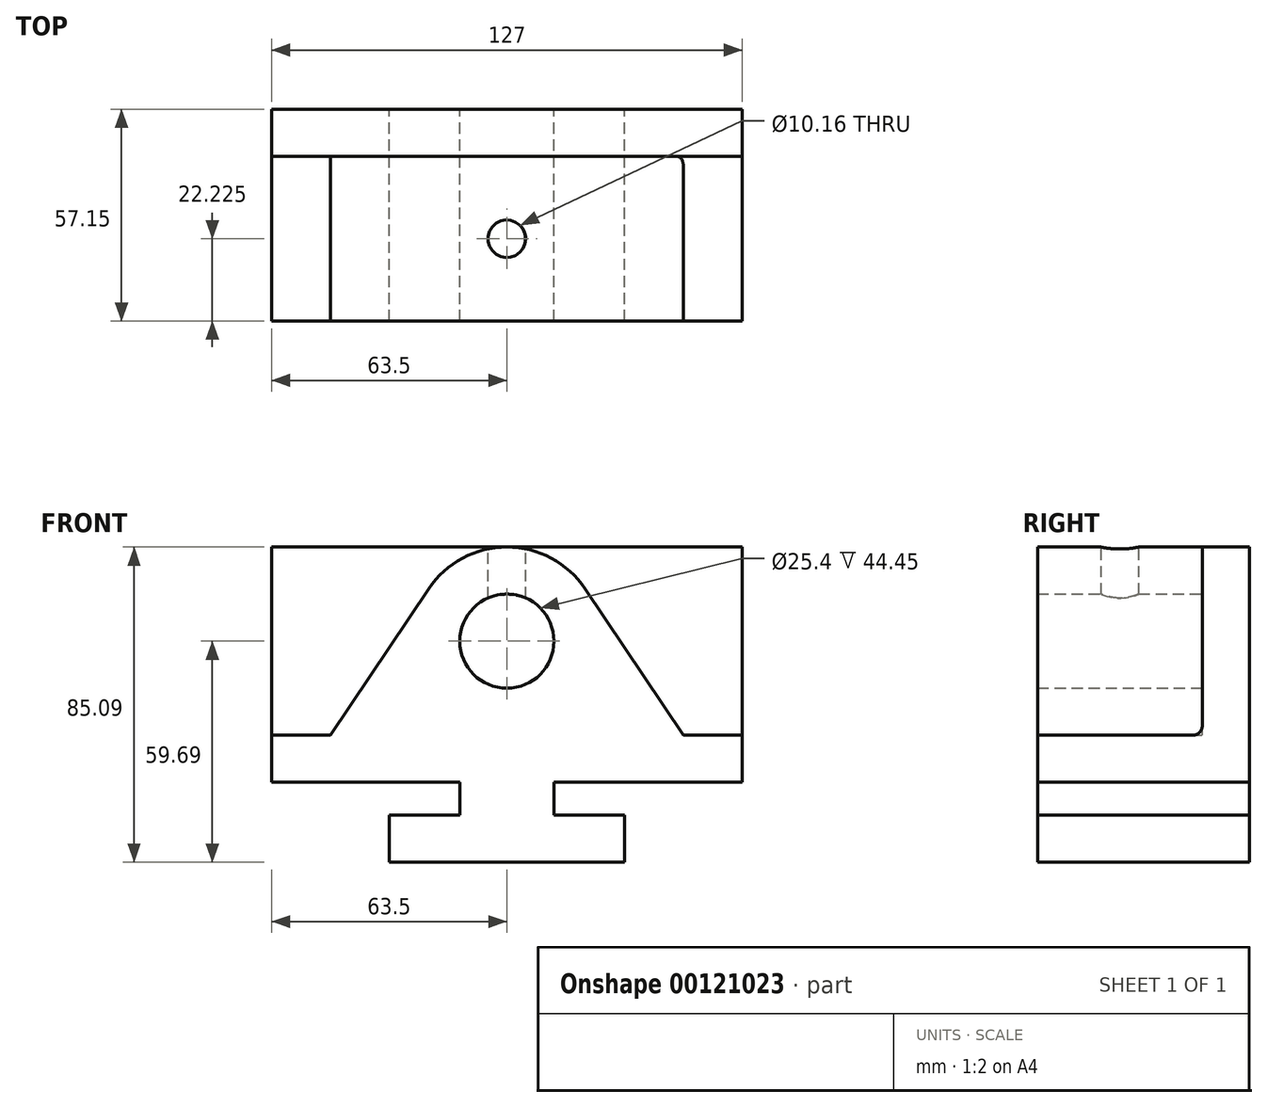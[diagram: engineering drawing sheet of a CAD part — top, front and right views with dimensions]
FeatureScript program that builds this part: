
annotation { "Feature Type Name" : "Feature", "Feature Type Description" : "" }
export const myFeature = defineFeature(function(context is Context, id is Id, definition is map)
    precondition{}
    {
        {
            var Q0;
            Q0=qCreatedBy(makeId("Front.planeOp"),FACE);
            var sketch = newSketch(context, id + "F0", { "sketchPlane" : qUnion([Q0])});
            skLineSegment(sketch, "E0", {"start": v(0, 47.91) * mm, "end": v(0, -62.83) * mm, "construction": true});
            skLineSegment(sketch, "E1", {"start": v(-31.75, 0) * mm, "end": v(31.75, 0) * mm});
            skLineSegment(sketch, "E2", {"start": v(31.75, 0) * mm, "end": v(31.75, 12.7) * mm});
            skLineSegment(sketch, "E3", {"start": v(31.75, 12.7) * mm, "end": v(12.7, 12.7) * mm});
            skLineSegment(sketch, "E4", {"start": v(12.7, 12.7) * mm, "end": v(12.7, 21.6) * mm});
            skLineSegment(sketch, "E5", {"start": v(12.7, 21.59) * mm, "end": v(63.5, 21.59) * mm});
            skLineSegment(sketch, "E6", {"start": v(63.5, 21.6) * mm, "end": v(63.5, 34.3) * mm});
            skLineSegment(sketch, "E7", {"start": v(63.5, 34.3) * mm, "end": v(47.62, 34.3) * mm});
            skLineSegment(sketch, "E8", {"start": v(47.63, 34.3) * mm, "end": v(21.1, 73.84) * mm});
            skLineSegment(sketch, "E9", {"start": v(-31.75, 0) * mm, "end": v(-31.75, 12.7) * mm});
            skLineSegment(sketch, "E10", {"start": v(-31.75, 12.7) * mm, "end": v(-12.7, 12.7) * mm});
            skLineSegment(sketch, "E11", {"start": v(-12.7, 12.7) * mm, "end": v(-12.7, 21.6) * mm});
            skLineSegment(sketch, "E12", {"start": v(-12.7, 21.6) * mm, "end": v(-63.5, 21.59) * mm});
            skLineSegment(sketch, "E13", {"start": v(-63.5, 21.59) * mm, "end": v(-63.5, 34.3) * mm});
            skLineSegment(sketch, "E14", {"start": v(-63.5, 34.3) * mm, "end": v(-47.62, 34.3) * mm});
            skLineSegment(sketch, "E15", {"start": v(-47.63, 34.3) * mm, "end": v(-21.1, 73.84) * mm});
            skArc(sketch, "E16", {"start": v(21.1, 73.84) * mm, "mid": v(0, 85.1) * mm, "end": v(-21.1, 73.84) * mm});
            skCircle(sketch, "E17", {"center": v(0, 59.7) * mm, "radius": 12.7 * mm});
            skPoint(sketch, "E18.startSnap0", {"position": v(0, 85.1) * mm});
            skPoint(sketch, "E19.endSnap0", {"position": v(-63.5, 27.94) * mm});
            skPoint(sketch, "E20.endSnap0", {"position": v(63.5, 27.94) * mm});
            skSolve(sketch);
        }
        {
            var Q0;
            {var subQ6=sQuery(id+"F0.wireOp",EDGE,"E7");Q0=makeQuery(id+"F0.imprint","IMPRINT",FACE,{"disambiguationData":[TD([[makeQuery(id+"F0.imprint","IMPRINT",EDGE,{"derivedFrom":subQ6}),1.0]])]});}
            var Q1;
            Q1=makeQuery(id+"F0.imprint","IMPRINT",FACE,{"disambiguationData":[TD([[makeQuery(id+"F0.imprint","IMPRINT",EDGE,{"derivedFrom":sQuery(id+"F0.wireOp",EDGE,"E1")}),1.0]])]});
            extrude(context, id + "F1", {"entities" : qUnion([Q0, Q1]), "depth" : 44.45 * mm});
        }
        {
            var Q0;
            Q0=makeQuery(id+"F0.imprint","IMPRINT",FACE,{"disambiguationData":[TD([[makeQuery(id+"F0.imprint","IMPRINT",EDGE,{"derivedFrom":sQuery(id+"F0.wireOp",EDGE,"E1")}),1.0]])]});
            cPlane(context, id + "F2", {"entities" : qUnion([Q0]), "cplaneType" : CPlaneType.OFFSET, "offset" : 0 * mm, "width" : 152.4 * mm, "height" : 152.4 * mm});
        }
        {
            var Q0;
            Q0=qCreatedBy(id+"F2.planeOp",FACE);
            var sketch = newSketch(context, id + "F3", { "sketchPlane" : qUnion([Q0])});
            skPoint(sketch, "E21.0", {"position": v(63.5, 21.6) * mm});
            skPoint(sketch, "E22.0", {"position": v(-63.5, 21.59) * mm});
            skPoint(sketch, "E23.0", {"position": v(0, 85.1) * mm});
            skLineSegment(sketch, "E24.bottom", {"start": v(63.5, 21.6) * mm, "end": v(-63.5, 21.6) * mm});
            skLineSegment(sketch, "E24.top", {"start": v(63.5, 85.1) * mm, "end": v(-63.5, 85.1) * mm});
            skLineSegment(sketch, "E24.left", {"start": v(63.5, 21.6) * mm, "end": v(63.5, 85.1) * mm});
            skLineSegment(sketch, "E24.right", {"start": v(-63.5, 21.6) * mm, "end": v(-63.5, 85.1) * mm});
            skLineSegment(sketch, "E25.0", {"start": v(-12.7, 12.7) * mm, "end": v(-12.7, 21.6) * mm});
            skLineSegment(sketch, "E25.1", {"start": v(12.7, 12.7) * mm, "end": v(12.7, 21.59) * mm});
            skLineSegment(sketch, "E25.2", {"start": v(31.75, 12.7) * mm, "end": v(12.7, 12.7) * mm});
            skLineSegment(sketch, "E25.3", {"start": v(31.75, 0) * mm, "end": v(31.75, 12.7) * mm});
            skLineSegment(sketch, "E25.4", {"start": v(-31.75, 0) * mm, "end": v(31.75, 0) * mm});
            skLineSegment(sketch, "E25.5", {"start": v(-31.75, 0) * mm, "end": v(-31.75, 12.7) * mm});
            skLineSegment(sketch, "E25.6", {"start": v(-31.75, 12.7) * mm, "end": v(-12.7, 12.7) * mm});
            skSolve(sketch);
        }
        {
            var Q0;
            Q0=qCreatedBy(makeId("Top.planeOp"),FACE);
            cPlane(context, id + "F4", {"entities" : qUnion([Q0]), "cplaneType" : CPlaneType.OFFSET, "offset" : 85.1 * mm, "width" : 152.4 * mm, "height" : 152.4 * mm});
        }
        {
            var Q0;
            Q0=qCreatedBy(id+"F4.planeOp",FACE);
            var sketch = newSketch(context, id + "F5", { "sketchPlane" : qUnion([Q0])});
            skLineSegment(sketch, "E26.0", {"start": v(21.1, 0) * mm, "end": v(-21.1, 0) * mm});
            skCircle(sketch, "E27", {"center": v(0, -22.23) * mm, "radius": 5.08 * mm});
            skPoint(sketch, "E27.centerSnap0", {"position": v(0, 0) * mm});
            skSolve(sketch);
        }
        {
            var Q0;
            Q0=makeQuery(id+"F5.imprint","IMPRINT",FACE,{"disambiguationData":[TD([[makeQuery(id+"F5.imprint","IMPRINT",EDGE,{"derivedFrom":sQuery(id+"F5.wireOp",EDGE,"E27")}),1.0]])]});
            extrude(context, id + "F6", {"entities" : qUnion([Q0]), "operationType" : NewBodyOperationType.REMOVE, "oppositeDirection" : true, "depth" : 25.4 * mm});
        }
        {
            var Q0;
            Q0=makeQuery(id+"F3.imprint","IMPRINT",FACE,{"disambiguationData":[TD([[makeQuery(id+"F3.imprint","IMPRINT",EDGE,{"derivedFrom":sQuery(id+"F3.wireOp",EDGE,"E24.bottom")}),-1.0]])]});
            extrude(context, id + "F7", {"entities" : qUnion([Q0]), "operationType" : NewBodyOperationType.ADD, "oppositeDirection" : true, "depth" : 12.7 * mm});
        }
        {
            var Q0;
            Q0=makeQuery(id+"F1.opExtrude","CAP_EDGE",EDGE,{"disambiguationData":[OSD([sQuery(id+"F0.wireOp",EDGE,"E14")])],"isStart":true});
            var Q1;
            Q1=makeQuery(id+"F1.opExtrude","CAP_EDGE",EDGE,{"disambiguationData":[OSD([sQuery(id+"F0.wireOp",EDGE,"E15")])],"isStart":true});
            var Q2;
            Q2=makeQuery(id+"F1.opExtrude","CAP_EDGE",EDGE,{"disambiguationData":[OSD([sQuery(id+"F0.wireOp",EDGE,"E7")])],"isStart":true});
            fillet(context, id + "F8", {"entities" : qUnion([Q0, Q1, Q2]), "radius" : 2.54 * mm, "tangentPropagation" : true, "allowEdgeOverflow" : false});
        }
        {
            var Q0;
            Q0=makeQuery(id+"F1.opExtrude","CAP_FACE",FACE,{"disambiguationData":[OSD([sQuery(id+"F0.wireOp",EDGE,"E1"),sQuery(id+"F0.wireOp",EDGE,"E2"),sQuery(id+"F0.wireOp",EDGE,"E3"),sQuery(id+"F0.wireOp",EDGE,"E4"),sQuery(id+"F0.wireOp",EDGE,"E5"),sQuery(id+"F0.wireOp",EDGE,"E6"),sQuery(id+"F0.wireOp",EDGE,"E7"),sQuery(id+"F0.wireOp",EDGE,"E8"),sQuery(id+"F0.wireOp",EDGE,"E9"),sQuery(id+"F0.wireOp",EDGE,"E10"),sQuery(id+"F0.wireOp",EDGE,"E11"),sQuery(id+"F0.wireOp",EDGE,"E12"),sQuery(id+"F0.wireOp",EDGE,"E13"),sQuery(id+"F0.wireOp",EDGE,"E14"),sQuery(id+"F0.wireOp",EDGE,"E15"),sQuery(id+"F0.wireOp",EDGE,"E16"),sQuery(id+"F0.wireOp",EDGE,"E17")])],"isStart":true});
            extrude(context, id + "F9", {"entities" : qUnion([Q0]), "operationType" : NewBodyOperationType.ADD, "depth" : 12.7 * mm});
        }
    });
